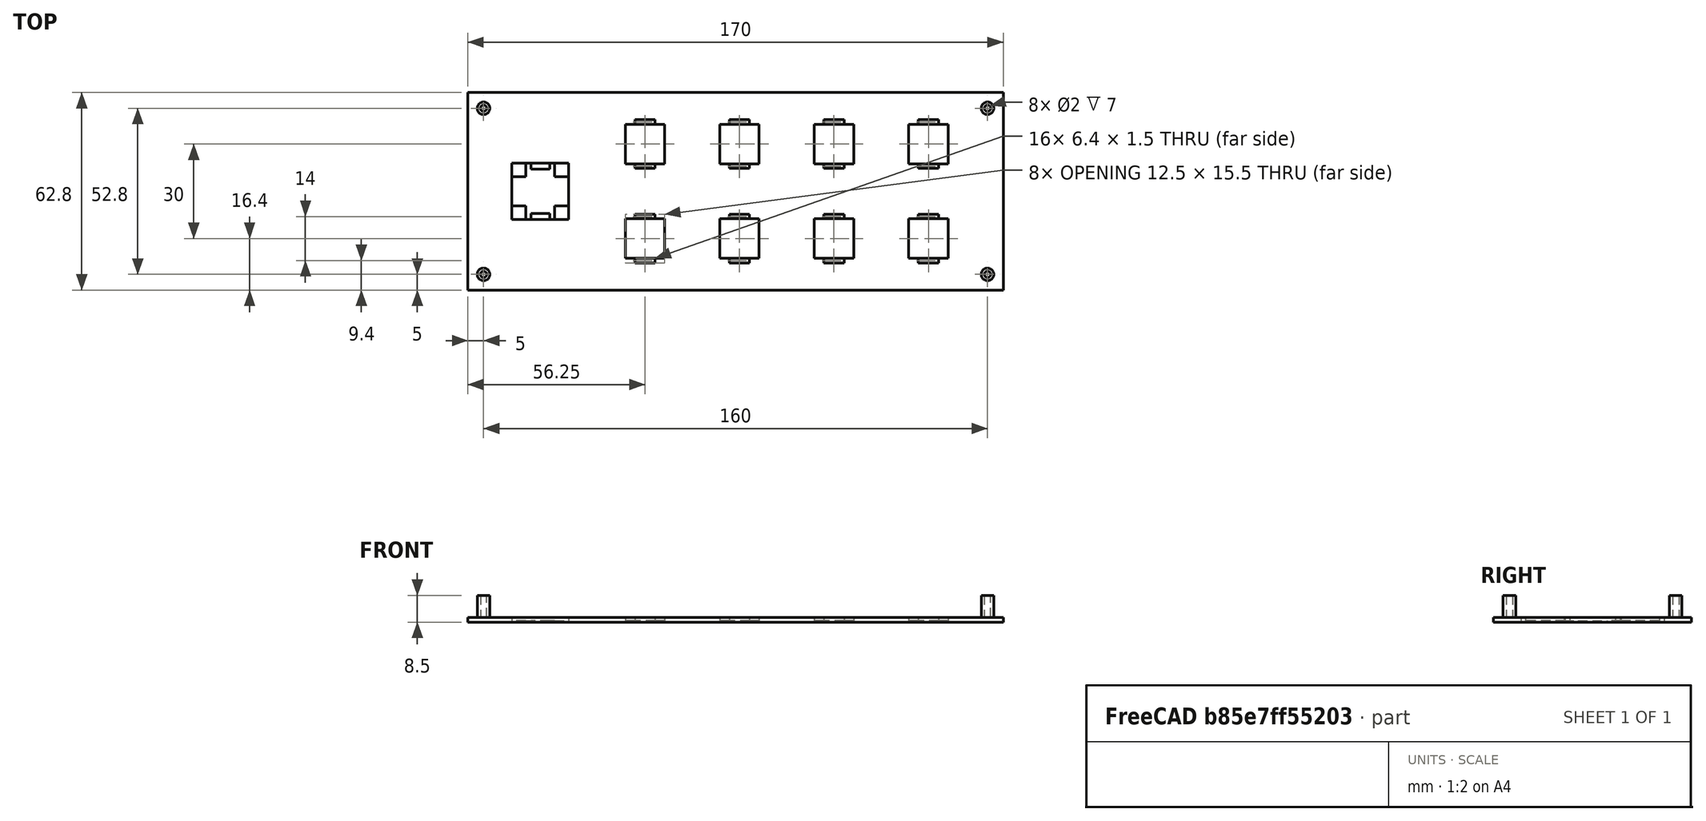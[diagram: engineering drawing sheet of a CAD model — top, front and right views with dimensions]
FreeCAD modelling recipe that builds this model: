
FCSTD DOCUMENT  (FreeCAD 0.20R28671 (Git))
Label: soporte botones atras
License: All rights reserved
LicenseURL: http://en.wikipedia.org/wiki/All_rights_reserved
objects: TechDraw::DrawViewDimension×23, Sketcher::SketchObject×6, PartDesign::Pocket×4, PartDesign::Pad×2, TechDraw::DrawProjGroupItem×2, PartDesign::LinearPattern×1, PartDesign::Body×1, Part::Refine×1, TechDraw::DrawProjGroup×1, TechDraw::DrawSVGTemplate×1, TechDraw::DrawViewAnnotation×1, TechDraw::DrawViewSymbol×1, TechDraw::DrawPage×1
note: 21 computed .brp shape members not serialized (recipe doc carries the construction recipe); baked Part::Feature solids carry a one-line shape summary decoded from their .brp

FEATURE [Sketcher::SketchObject] Sketch
  FullyConstrained = true
  MapMode = 5
  Support = -> [XY_Plane]
  sketch-geometry (12):
    g0: LineSegment StartX=0 StartY=0 StartZ=0 EndX=170 EndY=0 EndZ=0
    g1: LineSegment StartX=170 StartY=0 StartZ=0 EndX=170 EndY=62.8 EndZ=0
    g2: LineSegment StartX=170 StartY=62.8 StartZ=0 EndX=0 EndY=62.8 EndZ=0
    g3: LineSegment StartX=0 StartY=62.8 StartZ=0 EndX=0 EndY=0 EndZ=0
    g4: LineSegment StartX=14 StartY=40.4 StartZ=0 EndX=32 EndY=40.4 EndZ=0
    g5: LineSegment StartX=32 StartY=40.4 StartZ=0 EndX=32 EndY=22.4 EndZ=0
    g6: LineSegment StartX=32 StartY=22.4 StartZ=0 EndX=14 EndY=22.4 EndZ=0
    g7: LineSegment StartX=14 StartY=22.4 StartZ=0 EndX=14 EndY=40.4 EndZ=0
    g8: LineSegment StartX=14 StartY=40.4 StartZ=0 EndX=23 EndY=31.4 EndZ=0
    g9: LineSegment StartX=23 StartY=31.4 StartZ=0 EndX=32 EndY=22.4 EndZ=0
    g10: LineSegment StartX=0 StartY=0 StartZ=0 EndX=0 EndY=31.4 EndZ=0
    g11: LineSegment StartX=0 StartY=62.8 StartZ=0 EndX=0 EndY=31.4 EndZ=0
  constraints (33):
    c: Coincident(g0,g1)
    c: Coincident(g1,g2)
    c: Coincident(g2,g3)
    c: Coincident(g3,g0)
    c: Horizontal(g0)
    c: Horizontal(g2)
    c: Vertical(g1)
    c: Vertical(g3)
    c: Coincident(g0,g-1)
    c: DistanceY(g3,g3) = 62.8
    c: DistanceX(g0,g0) = 170
    c: Coincident(g4,g5)
    c: Coincident(g5,g6)
    c: Coincident(g6,g7)
    c: Coincident(g7,g4)
    c: Horizontal(g4)
    c: Horizontal(g6)
    c: Vertical(g5)
    c: Vertical(g7)
    c: Coincident(g8,g4)
    c: Coincident(g9,g8)
    c: Coincident(g9,g5)
    c: Parallel(g9,g8)
    c: Equal(g8,g9)
    c: Coincident(g10,g0)
    c: Coincident(g11,g2)
    c: Coincident(g11,g10)
    c: Horizontal(g10,g8)
    c: Equal(g6,g7)
    c: DistanceX(g6,g6) = 18
    c: Equal(g10,g11)
    c: Vertical(g10)
    c: DistanceX(g10,g6) = 14
FEATURE [PartDesign::Pad] Pad
  Direction = (0,0,1)
  Length = 1.5
  Length2 = 100
  Profile = -> Sketch
  ReferenceAxis = -> Sketch [N_Axis]
  Type = 0
FEATURE [Sketcher::SketchObject] Sketch001
  FullyConstrained = true
  MapMode = 5
  Placement = pos=(0,0,1.5) rot=(0,0,1;0rad)
  Support = -> [Pad]
  expr: Constraints[10] = Sketch.Constraints[10]
  expr: Constraints[29] = Sketch.Constraints[29]
  expr: Constraints[32] = Sketch.Constraints[32]
  expr: Constraints[9] = Sketch.Constraints[9]
  sketch-geometry (12):
    g0: LineSegment StartX=0 StartY=0 StartZ=0 EndX=170 EndY=0 EndZ=0
    g1: LineSegment StartX=170 StartY=0 StartZ=0 EndX=170 EndY=62.8 EndZ=0
    g2: LineSegment StartX=170 StartY=62.8 StartZ=0 EndX=0 EndY=62.8 EndZ=0
    g3: LineSegment StartX=0 StartY=62.8 StartZ=0 EndX=0 EndY=0 EndZ=0
    g4: LineSegment StartX=14 StartY=40.4 StartZ=0 EndX=32 EndY=40.4 EndZ=0
    g5: LineSegment StartX=32 StartY=40.4 StartZ=0 EndX=32 EndY=22.4 EndZ=0
    g6: LineSegment StartX=32 StartY=22.4 StartZ=0 EndX=14 EndY=22.4 EndZ=0
    g7: LineSegment StartX=14 StartY=22.4 StartZ=0 EndX=14 EndY=40.4 EndZ=0
    g8: LineSegment StartX=14 StartY=40.4 StartZ=0 EndX=23 EndY=31.4 EndZ=0
    g9: LineSegment StartX=23 StartY=31.4 StartZ=0 EndX=32 EndY=22.4 EndZ=0
    g10: LineSegment StartX=0 StartY=0 StartZ=0 EndX=0 EndY=31.4 EndZ=0
    g11: LineSegment StartX=0 StartY=62.8 StartZ=0 EndX=0 EndY=31.4 EndZ=0
  constraints (33):
    c: Coincident(g0,g1)
    c: Coincident(g1,g2)
    c: Coincident(g2,g3)
    c: Coincident(g3,g0)
    c: Horizontal(g0)
    c: Horizontal(g2)
    c: Vertical(g1)
    c: Vertical(g3)
    c: Coincident(g0,g-1)
    c: DistanceY(g3,g3) = 62.8
    c: DistanceX(g0,g0) = 170
    c: Coincident(g4,g5)
    c: Coincident(g5,g6)
    c: Coincident(g6,g7)
    c: Coincident(g7,g4)
    c: Horizontal(g4)
    c: Horizontal(g6)
    c: Vertical(g5)
    c: Vertical(g7)
    c: Coincident(g8,g4)
    c: Coincident(g9,g8)
    c: Coincident(g9,g5)
    c: Parallel(g9,g8)
    c: Equal(g8,g9)
    c: Coincident(g10,g0)
    c: Coincident(g11,g2)
    c: Coincident(g11,g10)
    c: Horizontal(g10,g8)
    c: Equal(g6,g7)
    c: DistanceX(g6,g6) = 18
    c: Equal(g10,g11)
    c: Vertical(g10)
    c: DistanceX(g10,g6) = 14
FEATURE [PartDesign::Pocket] Pocket
  BaseFeature = -> Pad
  Direction = (0,0,-1)
  Length = 1
  Length2 = 100
  Profile = -> Sketch001
  Type = 0
FEATURE [Sketcher::SketchObject] Sketch002
  ExternalGeometry = -> [Pocket]
  FullyConstrained = true
  MapMode = 5
  Placement = pos=(0,0,1.5) rot=(0,0,1;0rad)
  Support = -> [Pocket]
  sketch-geometry (25):
    g0: LineSegment StartX=50 StartY=52.65 StartZ=0 EndX=62.5 EndY=52.65 EndZ=0
    g1: LineSegment StartX=62.5 StartY=52.65 StartZ=0 EndX=62.5 EndY=40.15 EndZ=0
    g2: LineSegment StartX=62.5 StartY=40.15 StartZ=0 EndX=50 EndY=40.15 EndZ=0
    g3: LineSegment StartX=50 StartY=40.15 StartZ=0 EndX=50 EndY=52.65 EndZ=0
    g4: LineSegment StartX=80 StartY=52.65 StartZ=0 EndX=92.5 EndY=52.65 EndZ=0
    g5: LineSegment StartX=92.5 StartY=52.65 StartZ=0 EndX=92.5 EndY=40.15 EndZ=0
    g6: LineSegment StartX=80 StartY=40.15 StartZ=0 EndX=80 EndY=52.65 EndZ=0
    g7: LineSegment StartX=92.5 StartY=40.15 StartZ=0 EndX=80 EndY=40.15 EndZ=0
    g8: LineSegment StartX=50 StartY=52.65 StartZ=0 EndX=80 EndY=52.65 EndZ=0
    g9: LineSegment StartX=50 StartY=22.65 StartZ=0 EndX=62.5 EndY=22.65 EndZ=0
    g10: LineSegment StartX=62.5 StartY=22.65 StartZ=0 EndX=62.5 EndY=10.15 EndZ=0
    g11: LineSegment StartX=50 StartY=10.15 StartZ=0 EndX=50 EndY=22.65 EndZ=0
    g12: LineSegment StartX=62.5 StartY=10.15 StartZ=0 EndX=50 EndY=10.15 EndZ=0
    g13: LineSegment StartX=50 StartY=52.65 StartZ=0 EndX=50 EndY=22.65 EndZ=0
    g14: LineSegment StartX=80 StartY=22.65 StartZ=0 EndX=92.5 EndY=22.65 EndZ=0
    g15: LineSegment StartX=92.5 StartY=22.65 StartZ=0 EndX=92.5 EndY=10.15 EndZ=0
    g16: LineSegment StartX=80 StartY=10.15 StartZ=0 EndX=80 EndY=22.65 EndZ=0
    g17: LineSegment StartX=92.5 StartY=10.15 StartZ=0 EndX=80 EndY=10.15 EndZ=0
    g18: LineSegment StartX=50 StartY=22.65 StartZ=0 EndX=80 EndY=22.65 EndZ=0
    g19: LineSegment StartX=62.5 StartY=40.15 StartZ=0 EndX=62.5 EndY=31.4 EndZ=0
    g20: LineSegment StartX=62.5 StartY=31.4 StartZ=0 EndX=62.5 EndY=22.65 EndZ=0
    g21: LineSegment StartX=32 StartY=40.4 StartZ=0 EndX=32 EndY=31.4 EndZ=0
    g22: LineSegment StartX=32 StartY=31.4 StartZ=0 EndX=32 EndY=22.4 EndZ=0
    g23: LineSegment StartX=50 StartY=40.15 StartZ=0 EndX=32 EndY=40.15 EndZ=0
    g24: LineSegment StartX=32 StartY=40.4 StartZ=0 EndX=32 EndY=22.4 EndZ=0
  constraints (69):
    c: Coincident(g0,g1)
    c: Coincident(g1,g2)
    c: Coincident(g2,g3)
    c: Coincident(g3,g0)
    c: Horizontal(g0)
    c: Horizontal(g2)
    c: Vertical(g1)
    c: Vertical(g3)
    c: Equal(g0,g1)
    c: Coincident(g4,g5)
    c: Coincident(g5,g7)
    c: Coincident(g7,g6)
    c: Coincident(g6,g4)
    c: Horizontal(g4)
    c: Horizontal(g7)
    c: Vertical(g5)
    c: Vertical(g6)
    c: Equal(g4,g5)
    c: Coincident(g0,g8)
    c: Coincident(g4,g8)
    c: Angle(g8) = 0
    c: Coincident(g9,g10)
    c: Coincident(g10,g12)
    c: Coincident(g12,g11)
    c: Coincident(g11,g9)
    c: Horizontal(g9)
    c: Horizontal(g12)
    c: Vertical(g10)
    c: Vertical(g11)
    c: DistanceX(g12,g12) = 12.5
    c: Equal(g9,g10)
    c: Coincident(g0,g13)
    c: Coincident(g9,g13)
    c: Perpendicular(g13,g8)
    c: Coincident(g14,g15)
    c: Coincident(g15,g17)
    c: Coincident(g17,g16)
    c: Coincident(g16,g14)
    c: Horizontal(g14)
    c: Horizontal(g17)
    c: Vertical(g15)
    c: Vertical(g16)
    c: Equal(g14,g15)
    c: Coincident(g9,g18)
    c: Coincident(g14,g18)
    c: Equal(g8,g18)
    c: Parallel(g18,g8)
    c: Vertical(g14,g5)
    c: Vertical(g1,g9)
    c: Coincident(g19,g1)
    c: Coincident(g20,g19)
    c: Coincident(g20,g9)
    c: Equal(g20,g19)
    c: Vertical(g20)
    c: Equal(g17,g12)
    c: DistanceY(g11,g2) = 30
    c: DistanceX(g11,g16) = 30
    c: Coincident(g21,g-3)
    c: Coincident(g22,g21)
    c: Coincident(g22,g-4)
    c: Horizontal(g21,g19)
    c: Equal(g22,g21)
    c: Vertical(g22)
    c: Coincident(g23,g2)
    c: Horizontal(g23)
    c: PointOnObject(g23,g21)
    c: Coincident(g24,g21)
    c: Equal(g24,g23)
    c: Coincident(g24,g22)
FEATURE [PartDesign::Pocket] Pocket001
  BaseFeature = -> Pocket
  Direction = (0,0,-1)
  Length = 1
  Length2 = 100
  Profile = -> Sketch002
  Type = 0
FEATURE [PartDesign::LinearPattern] LinearPattern
  BaseFeature = -> Pocket001
  Direction = -> Sketch002 [Axis0]
  Length = 60
  Occurrences = 2
  Originals = -> [Pocket001]
  Overlap = 0
FEATURE [Sketcher::SketchObject] Sketch003
  ExternalGeometry = -> [LinearPattern]
  FullyConstrained = true
  MapMode = 5
  Placement = pos=(0,0,1.5) rot=(0,0,1;0rad)
  Support = -> [LinearPattern]
  sketch-geometry (16):
    g0: Circle CenterX=5 CenterY=5 CenterZ=0 NormalX=0 NormalY=0 NormalZ=1 AngleXU=0 Radius=1
    g1: Circle CenterX=5 CenterY=5 CenterZ=0 NormalX=0 NormalY=0 NormalZ=1 AngleXU=0 Radius=2
    g2: Circle CenterX=5 CenterY=57.8 CenterZ=0 NormalX=0 NormalY=0 NormalZ=1 AngleXU=0 Radius=1
    g3: Circle CenterX=5 CenterY=57.8 CenterZ=0 NormalX=0 NormalY=0 NormalZ=1 AngleXU=0 Radius=2
    g4: Circle CenterX=165 CenterY=57.8 CenterZ=0 NormalX=0 NormalY=0 NormalZ=1 AngleXU=0 Radius=2
    g5: Circle CenterX=165 CenterY=57.8 CenterZ=0 NormalX=0 NormalY=0 NormalZ=1 AngleXU=0 Radius=1
    g6: Circle CenterX=165 CenterY=5 CenterZ=0 NormalX=0 NormalY=0 NormalZ=1 AngleXU=0 Radius=2
    g7: Circle CenterX=165 CenterY=5 CenterZ=0 NormalX=0 NormalY=0 NormalZ=1 AngleXU=0 Radius=1
    g8: LineSegment StartX=0 StartY=0 StartZ=0 EndX=5 EndY=0 EndZ=0
    g9: LineSegment StartX=5 StartY=0 StartZ=0 EndX=5 EndY=5 EndZ=0
    g10: LineSegment StartX=165 StartY=5 StartZ=0 EndX=165 EndY=0 EndZ=0
    g11: LineSegment StartX=165 StartY=0 StartZ=0 EndX=170 EndY=0 EndZ=0
    g12: LineSegment StartX=165 StartY=57.8 StartZ=0 EndX=165 EndY=62.8 EndZ=0
    g13: LineSegment StartX=165 StartY=62.8 StartZ=0 EndX=170 EndY=62.8 EndZ=0
    g14: LineSegment StartX=5 StartY=57.8 StartZ=0 EndX=0 EndY=57.8 EndZ=0
    g15: LineSegment StartX=0 StartY=57.8 StartZ=0 EndX=0 EndY=62.8 EndZ=0
  constraints (40):
    c: Coincident(g1,g0)
    c: Diameter(g0) = 2
    c: Diameter(g1) = 4
    c: DistanceY(g-1,g0) = 5
    c: DistanceX(g-1,g0) = 5
    c: Coincident(g3,g2)
    c: Coincident(g5,g4)
    c: Coincident(g7,g6)
    c: Equal(g2,g5)
    c: Equal(g5,g7)
    c: Equal(g7,g0)
    c: Equal(g1,g6)
    c: Equal(g6,g4)
    c: Equal(g4,g3)
    c: Coincident(g8,g-1)
    c: PointOnObject(g8,g-1)
    c: Coincident(g9,g8)
    c: Coincident(g9,g0)
    c: Vertical(g9)
    c: Coincident(g10,g6)
    c: PointOnObject(g10,g-1)
    c: Vertical(g10)
    c: Coincident(g11,g10)
    c: Coincident(g11,g-5)
    c: Coincident(g12,g4)
    c: Vertical(g12)
    c: Coincident(g13,g12)
    c: Coincident(g13,g-4)
    c: Horizontal(g13)
    c: Coincident(g14,g2)
    c: PointOnObject(g14,g-2)
    c: Horizontal(g14)
    c: Coincident(g15,g14)
    c: Coincident(g15,g-3)
    c: Equal(g14,g15)
    c: Equal(g15,g8)
    c: Equal(g11,g10)
    c: Equal(g10,g13)
    c: Equal(g13,g12)
    c: Equal(g12,g8)
FEATURE [PartDesign::Pad] Pad001
  BaseFeature = -> LinearPattern
  Direction = (0,0,1)
  Length = 7
  Length2 = 100
  Profile = -> Sketch003
  ReferenceAxis = -> Sketch003 [N_Axis]
  Type = 0
FEATURE [Sketcher::SketchObject] Sketch004
  ExternalGeometry = -> [Pad001]
  FullyConstrained = true
  MapMode = 5
  Placement = pos=(0,0,1.5) rot=(0,0,1;0rad)
  Support = -> [Pad001]
  sketch-geometry (73):
    g0: LineSegment StartX=53.05 StartY=54.15 StartZ=0 EndX=59.45 EndY=54.15 EndZ=0
    g1: LineSegment StartX=59.45 StartY=54.15 StartZ=0 EndX=59.45 EndY=52.65 EndZ=0
    g2: LineSegment StartX=59.45 StartY=52.65 StartZ=0 EndX=53.05 EndY=52.65 EndZ=0
    g3: LineSegment StartX=53.05 StartY=52.65 StartZ=0 EndX=53.05 EndY=54.15 EndZ=0
    g4: LineSegment StartX=53.05 StartY=40.15 StartZ=0 EndX=59.45 EndY=40.15 EndZ=0
    g5: LineSegment StartX=59.45 StartY=40.15 StartZ=0 EndX=59.45 EndY=38.65 EndZ=0
    g6: LineSegment StartX=59.45 StartY=38.65 StartZ=0 EndX=53.05 EndY=38.65 EndZ=0
    g7: LineSegment StartX=53.05 StartY=38.65 StartZ=0 EndX=53.05 EndY=40.15 EndZ=0
    g8: LineSegment StartX=53.05 StartY=52.65 StartZ=0 EndX=50 EndY=52.65 EndZ=0
    g9: LineSegment StartX=62.5 StartY=52.65 StartZ=0 EndX=59.45 EndY=52.65 EndZ=0
    g10: LineSegment StartX=83.05 StartY=38.65 StartZ=0 EndX=83.05 EndY=40.15 EndZ=0
    g11: LineSegment StartX=89.45 StartY=38.65 StartZ=0 EndX=83.05 EndY=38.65 EndZ=0
    g12: LineSegment StartX=89.45 StartY=40.15 StartZ=0 EndX=89.45 EndY=38.65 EndZ=0
    g13: LineSegment StartX=83.05 StartY=40.15 StartZ=0 EndX=89.45 EndY=40.15 EndZ=0
    g14: LineSegment StartX=89.45 StartY=52.65 StartZ=0 EndX=83.05 EndY=52.65 EndZ=0
    g15: LineSegment StartX=83.05 StartY=54.15 StartZ=0 EndX=89.45 EndY=54.15 EndZ=0
    g16: LineSegment StartX=89.45 StartY=54.15 StartZ=0 EndX=89.45 EndY=52.65 EndZ=0
    g17: LineSegment StartX=83.05 StartY=52.65 StartZ=0 EndX=83.05 EndY=54.15 EndZ=0
    g18: LineSegment StartX=53.05 StartY=38.65 StartZ=0 EndX=83.05 EndY=38.65 EndZ=0
    g19: LineSegment StartX=113.05 StartY=38.65 StartZ=0 EndX=113.05 EndY=40.15 EndZ=0
    g20: LineSegment StartX=119.45 StartY=38.65 StartZ=0 EndX=113.05 EndY=38.65 EndZ=0
    g21: LineSegment StartX=119.45 StartY=40.15 StartZ=0 EndX=119.45 EndY=38.65 EndZ=0
    g22: LineSegment StartX=113.05 StartY=40.15 StartZ=0 EndX=119.45 EndY=40.15 EndZ=0
    g23: LineSegment StartX=119.45 StartY=52.65 StartZ=0 EndX=113.05 EndY=52.65 EndZ=0
    g24: LineSegment StartX=113.05 StartY=54.15 StartZ=0 EndX=119.45 EndY=54.15 EndZ=0
    g25: LineSegment StartX=119.45 StartY=54.15 StartZ=0 EndX=119.45 EndY=52.65 EndZ=0
    g26: LineSegment StartX=113.05 StartY=52.65 StartZ=0 EndX=113.05 EndY=54.15 EndZ=0
    g27: LineSegment StartX=83.05 StartY=38.65 StartZ=0 EndX=113.05 EndY=38.65 EndZ=0
    g28: LineSegment StartX=143.05 StartY=38.65 StartZ=0 EndX=143.05 EndY=40.15 EndZ=0
    g29: LineSegment StartX=149.45 StartY=38.65 StartZ=0 EndX=143.05 EndY=38.65 EndZ=0
    g30: LineSegment StartX=149.45 StartY=40.15 StartZ=0 EndX=149.45 EndY=38.65 EndZ=0
    g31: LineSegment StartX=143.05 StartY=40.15 StartZ=0 EndX=149.45 EndY=40.15 EndZ=0
    g32: LineSegment StartX=149.45 StartY=52.65 StartZ=0 EndX=143.05 EndY=52.65 EndZ=0
    g33: LineSegment StartX=143.05 StartY=54.15 StartZ=0 EndX=149.45 EndY=54.15 EndZ=0
    g34: LineSegment StartX=149.45 StartY=54.15 StartZ=0 EndX=149.45 EndY=52.65 EndZ=0
    g35: LineSegment StartX=143.05 StartY=52.65 StartZ=0 EndX=143.05 EndY=54.15 EndZ=0
    g36: LineSegment StartX=113.05 StartY=38.65 StartZ=0 EndX=143.05 EndY=38.65 EndZ=0
    g37: LineSegment StartX=83.05 StartY=40.15 StartZ=0 EndX=80 EndY=40.15 EndZ=0
    g38: LineSegment StartX=32 StartY=40.4 StartZ=0 EndX=32 EndY=31.4 EndZ=0
    g39: LineSegment StartX=32 StartY=31.4 StartZ=0 EndX=32 EndY=22.4 EndZ=0
    g40: LineSegment StartX=32 StartY=31.4 StartZ=0 EndX=170 EndY=31.4 EndZ=0
    g41: LineSegment StartX=59.45 StartY=24.15 StartZ=0 EndX=53.05 EndY=24.15 EndZ=0
    g42: LineSegment StartX=53.05 StartY=24.15 StartZ=0 EndX=53.05 EndY=22.65 EndZ=0
    g43: LineSegment StartX=53.05 StartY=22.65 StartZ=0 EndX=59.45 EndY=22.65 EndZ=0
    g44: LineSegment StartX=59.45 StartY=22.65 StartZ=0 EndX=59.45 EndY=24.15 EndZ=0
    g45: LineSegment StartX=53.05 StartY=8.65 StartZ=0 EndX=59.45 EndY=8.65 EndZ=0
    g46: LineSegment StartX=59.45 StartY=8.65 StartZ=0 EndX=59.45 EndY=10.15 EndZ=0
    g47: LineSegment StartX=59.45 StartY=10.15 StartZ=0 EndX=53.05 EndY=10.15 EndZ=0
    g48: LineSegment StartX=53.05 StartY=10.15 StartZ=0 EndX=53.05 EndY=8.65 EndZ=0
    g49: LineSegment StartX=83.05 StartY=8.65 StartZ=0 EndX=89.45 EndY=8.65 EndZ=0
    g50: LineSegment StartX=83.05 StartY=10.15 StartZ=0 EndX=83.05 EndY=8.65 EndZ=0
    g51: LineSegment StartX=89.45 StartY=10.15 StartZ=0 EndX=83.05 EndY=10.15 EndZ=0
    g52: LineSegment StartX=89.45 StartY=8.65 StartZ=0 EndX=89.45 EndY=10.15 EndZ=0
    g53: LineSegment StartX=83.05 StartY=22.65 StartZ=0 EndX=89.45 EndY=22.65 EndZ=0
    g54: LineSegment StartX=89.45 StartY=24.15 StartZ=0 EndX=83.05 EndY=24.15 EndZ=0
    g55: LineSegment StartX=83.05 StartY=24.15 StartZ=0 EndX=83.05 EndY=22.65 EndZ=0
    g56: LineSegment StartX=89.45 StartY=22.65 StartZ=0 EndX=89.45 EndY=24.15 EndZ=0
    g57: LineSegment StartX=113.05 StartY=8.65 StartZ=0 EndX=119.45 EndY=8.65 EndZ=0
    g58: LineSegment StartX=119.45 StartY=10.15 StartZ=0 EndX=113.05 EndY=10.15 EndZ=0
    g59: LineSegment StartX=113.05 StartY=10.15 StartZ=0 EndX=113.05 EndY=8.65 EndZ=0
    g60: LineSegment StartX=119.45 StartY=8.65 StartZ=0 EndX=119.45 EndY=10.15 EndZ=0
    g61: LineSegment StartX=113.05 StartY=22.65 StartZ=0 EndX=119.45 EndY=22.65 EndZ=0
    g62: LineSegment StartX=119.45 StartY=22.65 StartZ=0 EndX=119.45 EndY=24.15 EndZ=0
    g63: LineSegment StartX=119.45 StartY=24.15 StartZ=0 EndX=113.05 EndY=24.15 EndZ=0
    g64: LineSegment StartX=113.05 StartY=24.15 StartZ=0 EndX=113.05 EndY=22.65 EndZ=0
    g65: LineSegment StartX=143.05 StartY=8.65 StartZ=0 EndX=149.45 EndY=8.65 EndZ=0
    g66: LineSegment StartX=149.45 StartY=10.15 StartZ=0 EndX=143.05 EndY=10.15 EndZ=0
    g67: LineSegment StartX=143.05 StartY=10.15 StartZ=0 EndX=143.05 EndY=8.65 EndZ=0
    g68: LineSegment StartX=149.45 StartY=8.65 StartZ=0 EndX=149.45 EndY=10.15 EndZ=0
    g69: LineSegment StartX=143.05 StartY=22.65 StartZ=0 EndX=149.45 EndY=22.65 EndZ=0
    g70: LineSegment StartX=143.05 StartY=24.15 StartZ=0 EndX=143.05 EndY=22.65 EndZ=0
    g71: LineSegment StartX=149.45 StartY=24.15 StartZ=0 EndX=143.05 EndY=24.15 EndZ=0
    g72: LineSegment StartX=149.45 StartY=22.65 StartZ=0 EndX=149.45 EndY=24.15 EndZ=0
  constraints (212):
    c: Coincident(g0,g1)
    c: Coincident(g1,g2)
    c: Coincident(g2,g3)
    c: Coincident(g3,g0)
    c: Horizontal(g0)
    c: Horizontal(g2)
    c: Vertical(g1)
    c: Vertical(g3)
    c: Coincident(g4,g5)
    c: Coincident(g5,g6)
    c: Coincident(g6,g7)
    c: Coincident(g7,g4)
    c: Horizontal(g4)
    c: Horizontal(g6)
    c: Vertical(g5)
    c: Vertical(g7)
    c: Vertical(g2,g4)
    c: Vertical(g4,g1)
    c: Equal(g7,g3)
    c: Coincident(g8,g2)
    c: Coincident(g8,g-3)
    c: Coincident(g9,g-4)
    c: Coincident(g9,g1)
    c: Equal(g8,g9)
    c: Horizontal(g9)
    c: DistanceX(g0,g0) = 6.4
    c: DistanceY(g3,g3) = 1.5
    c: Horizontal(g4,g-6)
    c: Coincident(g15,g16)
    c: Coincident(g16,g14)
    c: Coincident(g14,g17)
    c: Coincident(g17,g15)
    c: Horizontal(g15)
    c: Horizontal(g14)
    c: Vertical(g16)
    c: Vertical(g17)
    c: Coincident(g13,g12)
    c: Coincident(g12,g11)
    c: Coincident(g11,g10)
    c: Coincident(g10,g13)
    c: Horizontal(g13)
    c: Horizontal(g11)
    c: Vertical(g12)
    c: Vertical(g10)
    c: Vertical(g14,g13)
    c: Vertical(g13,g16)
    c: Equal(g10,g17)
    c: Coincident(g7,g18)
    c: Coincident(g10,g18)
    c: Coincident(g24,g25)
    c: Coincident(g25,g23)
    c: Coincident(g23,g26)
    c: Coincident(g26,g24)
    c: Horizontal(g24)
    c: Horizontal(g23)
    c: Vertical(g25)
    c: Vertical(g26)
    c: Coincident(g22,g21)
    c: Coincident(g21,g20)
    c: Coincident(g20,g19)
    c: Coincident(g19,g22)
    c: Horizontal(g22)
    c: Horizontal(g20)
    c: Vertical(g21)
    c: Vertical(g19)
    c: Vertical(g23,g22)
    c: Vertical(g22,g25)
    c: Equal(g19,g26)
    c: Coincident(g10,g27)
    c: Coincident(g19,g27)
    c: Equal(g18,g27)
    c: Parallel(g27,g18)
    c: Coincident(g33,g34)
    c: Coincident(g34,g32)
    c: Coincident(g32,g35)
    c: Coincident(g35,g33)
    c: Horizontal(g33)
    c: Horizontal(g32)
    c: Vertical(g34)
    c: Vertical(g35)
    c: Coincident(g31,g30)
    c: Coincident(g30,g29)
    c: Coincident(g29,g28)
    c: Coincident(g28,g31)
    c: Horizontal(g31)
    c: Horizontal(g29)
    c: Vertical(g30)
    c: Vertical(g28)
    c: Vertical(g32,g31)
    c: Vertical(g31,g34)
    c: Equal(g28,g35)
    c: Coincident(g19,g36)
    c: Coincident(g28,g36)
    c: Equal(g18,g36)
    c: Parallel(g36,g18)
    c: Coincident(g37,g10)
    c: Coincident(g37,g-7)
    c: Equal(g37,g9)
    c: Horizontal(g37)
    c: Equal(g15,g0)
    c: Equal(g0,g24)
    c: Equal(g24,g33)
    c: Horizontal(g36)
    c: Equal(g12,g19)
    c: Equal(g19,g30)
    c: Horizontal(g14,g9)
    c: Horizontal(g23,g32)
    c: Horizontal(g23,g14)
    c: Coincident(g38,g-8)
    c: Coincident(g39,g38)
    c: Coincident(g39,g-9)
    c: Equal(g39,g38)
    c: Vertical(g39)
    c: Coincident(g40,g38)
    c: Horizontal(g40)
    c: Vertical(g-10,g40)
    c: Coincident(g45,g46)
    c: Coincident(g46,g47)
    c: Coincident(g47,g48)
    c: Coincident(g48,g45)
    c: Horizontal(g45)
    c: Horizontal(g47)
    c: Vertical(g46)
    c: Vertical(g48)
    c: Coincident(g43,g44)
    c: Coincident(g44,g41)
    c: Coincident(g41,g42)
    c: Coincident(g42,g43)
    c: Horizontal(g43)
    c: Horizontal(g41)
    c: Vertical(g44)
    c: Vertical(g42)
    c: Equal(g42,g48)
    c: Coincident(g49,g52)
    c: Coincident(g52,g51)
    c: Coincident(g51,g50)
    c: Coincident(g50,g49)
    c: Horizontal(g49)
    c: Horizontal(g51)
    c: Vertical(g52)
    c: Vertical(g50)
    c: Coincident(g53,g56)
    c: Coincident(g56,g54)
    c: Coincident(g54,g55)
    c: Coincident(g55,g53)
    c: Horizontal(g53)
    c: Horizontal(g54)
    c: Vertical(g56)
    c: Vertical(g55)
    c: Equal(g55,g50)
    c: Coincident(g57,g60)
    c: Coincident(g60,g58)
    c: Coincident(g58,g59)
    c: Coincident(g59,g57)
    c: Horizontal(g57)
    c: Horizontal(g58)
    c: Vertical(g60)
    c: Vertical(g59)
    c: Coincident(g61,g62)
    c: Coincident(g62,g63)
    c: Coincident(g63,g64)
    c: Coincident(g64,g61)
    c: Horizontal(g61)
    c: Horizontal(g63)
    c: Vertical(g62)
    c: Equal(g64,g59)
    c: Coincident(g65,g68)
    c: Coincident(g68,g66)
    c: Coincident(g66,g67)
    c: Coincident(g67,g65)
    c: Horizontal(g65)
    c: Horizontal(g66)
    c: Vertical(g68)
    c: Vertical(g67)
    c: Coincident(g69,g72)
    c: Coincident(g72,g71)
    c: Coincident(g71,g70)
    c: Coincident(g70,g69)
    c: Horizontal(g69)
    c: Horizontal(g71)
    c: Vertical(g72)
    c: Vertical(g70)
    c: Equal(g70,g67)
    c: Equal(g49,g45)
    c: Equal(g45,g57)
    c: Equal(g57,g65)
    c: Equal(g56,g64)
    c: Equal(g64,g72)
    c: Vertical(g41,g6)
    c: Vertical(g54,g10)
    c: Vertical(g63,g19)
    c: Vertical(g70,g28)
    c: Equal(g31,g71)
    c: Equal(g71,g63)
    c: Equal(g63,g54)
    c: Equal(g54,g41)
    c: Equal(g44,g55)
    c: Equal(g55,g62)
    c: Equal(g72,g30)
    c: Horizontal(g43,g-11)
    c: Horizontal(g-11,g53)
    c: Horizontal(g53,g61)
    c: Horizontal(g61,g69)
    c: Horizontal(g46,g-12)
    c: Vertical(g46,g43)
    c: Equal(g47,g43)
    c: Horizontal(g-12,g50)
    c: Horizontal(g51,g58)
    c: Horizontal(g58,g66)
    c: Vertical(g51,g53)
    c: Vertical(g61,g58)
    c: Vertical(g69,g66)
FEATURE [Sketcher::SketchObject] Sketch005
  ExternalGeometry = -> [Pad001]
  FullyConstrained = true
  MapMode = 5
  Placement = pos=(0,0,0.5) rot=(0,0,1;0rad)
  Support = -> [Pad001]
  sketch-geometry (26):
    g0: LineSegment StartX=20 StartY=40.4 StartZ=0 EndX=26 EndY=40.4 EndZ=0
    g1: LineSegment StartX=26 StartY=40.4 StartZ=0 EndX=26 EndY=38.4 EndZ=0
    g2: LineSegment StartX=26 StartY=38.4 StartZ=0 EndX=20 EndY=38.4 EndZ=0
    g3: LineSegment StartX=20 StartY=38.4 StartZ=0 EndX=20 EndY=40.4 EndZ=0
    g4: LineSegment StartX=20 StartY=22.4 StartZ=0 EndX=26 EndY=22.4 EndZ=0
    g5: LineSegment StartX=26 StartY=22.4 StartZ=0 EndX=26 EndY=24.4 EndZ=0
    g6: LineSegment StartX=26 StartY=24.4 StartZ=0 EndX=20 EndY=24.4 EndZ=0
    g7: LineSegment StartX=20 StartY=24.4 StartZ=0 EndX=20 EndY=22.4 EndZ=0
    g8: LineSegment StartX=20 StartY=40.4 StartZ=0 EndX=14 EndY=40.4 EndZ=0
    g9: LineSegment StartX=26 StartY=40.4 StartZ=0 EndX=32 EndY=40.4 EndZ=0
    g10: LineSegment StartX=14 StartY=40.4 StartZ=0 EndX=18.4 EndY=40.4 EndZ=0
    g11: LineSegment StartX=18.4 StartY=40.4 StartZ=0 EndX=18.4 EndY=36 EndZ=0
    g12: LineSegment StartX=18.4 StartY=36 StartZ=0 EndX=14 EndY=36 EndZ=0
    g13: LineSegment StartX=14 StartY=36 StartZ=0 EndX=14 EndY=40.4 EndZ=0
    g14: LineSegment StartX=32 StartY=40.4 StartZ=0 EndX=27.6 EndY=40.4 EndZ=0
    g15: LineSegment StartX=27.6 StartY=40.4 StartZ=0 EndX=27.6 EndY=36 EndZ=0
    g16: LineSegment StartX=27.6 StartY=36 StartZ=0 EndX=32 EndY=36 EndZ=0
    g17: LineSegment StartX=32 StartY=36 StartZ=0 EndX=32 EndY=40.4 EndZ=0
    g18: LineSegment StartX=14 StartY=22.4 StartZ=0 EndX=18.4 EndY=22.4 EndZ=0
    g19: LineSegment StartX=18.4 StartY=22.4 StartZ=0 EndX=18.4 EndY=26.8 EndZ=0
    g20: LineSegment StartX=18.4 StartY=26.8 StartZ=0 EndX=14 EndY=26.8 EndZ=0
    g21: LineSegment StartX=14 StartY=26.8 StartZ=0 EndX=14 EndY=22.4 EndZ=0
    g22: LineSegment StartX=32 StartY=22.4 StartZ=0 EndX=27.6 EndY=22.4 EndZ=0
    g23: LineSegment StartX=27.6 StartY=22.4 StartZ=0 EndX=27.6 EndY=26.8 EndZ=0
    g24: LineSegment StartX=27.6 StartY=26.8 StartZ=0 EndX=32 EndY=26.8 EndZ=0
    g25: LineSegment StartX=32 StartY=26.8 StartZ=0 EndX=32 EndY=22.4 EndZ=0
  constraints (72):
    c: Coincident(g0,g1)
    c: Coincident(g1,g2)
    c: Coincident(g2,g3)
    c: Coincident(g3,g0)
    c: Horizontal(g0)
    c: Horizontal(g2)
    c: Vertical(g1)
    c: Vertical(g3)
    c: Coincident(g4,g5)
    c: Coincident(g5,g6)
    c: Coincident(g6,g7)
    c: Coincident(g7,g4)
    c: Horizontal(g4)
    c: Horizontal(g6)
    c: Vertical(g5)
    c: Vertical(g7)
    c: Vertical(g6,g2)
    c: Vertical(g5,g1)
    c: DistanceX(g2,g2) = 6
    c: DistanceY(g3,g3) = 2
    c: Coincident(g8,g0)
    c: Coincident(g8,g-3)
    c: Horizontal(g8)
    c: Coincident(g9,g0)
    c: Coincident(g9,g-4)
    c: Equal(g9,g8)
    c: Equal(g5,g1)
    c: Horizontal(g4,g-5)
    c: Coincident(g10,g11)
    c: Coincident(g11,g12)
    c: Coincident(g12,g13)
    c: Coincident(g13,g10)
    c: Horizontal(g10)
    c: Horizontal(g12)
    c: Vertical(g11)
    c: Vertical(g13)
    c: Coincident(g10,g8)
    c: Coincident(g14,g15)
    c: Coincident(g15,g16)
    c: Coincident(g16,g17)
    c: Coincident(g17,g14)
    c: Horizontal(g14)
    c: Horizontal(g16)
    c: Vertical(g15)
    c: Vertical(g17)
    c: Coincident(g14,g9)
    c: Coincident(g18,g19)
    c: Coincident(g19,g20)
    c: Coincident(g20,g21)
    c: Coincident(g21,g18)
    c: Horizontal(g18)
    c: Horizontal(g20)
    c: Vertical(g19)
    c: Vertical(g21)
    c: Coincident(g18,g-6)
    c: Coincident(g22,g23)
    c: Coincident(g23,g24)
    c: Coincident(g24,g25)
    c: Coincident(g25,g22)
    c: Horizontal(g22)
    c: Horizontal(g24)
    c: Vertical(g23)
    c: Vertical(g25)
    c: Coincident(g22,g-5)
    c: Equal(g16,g15)
    c: Equal(g15,g12)
    c: Equal(g12,g11)
    c: Equal(g11,g20)
    c: Equal(g20,g19)
    c: Equal(g19,g23)
    c: Equal(g23,g24)
    c: DistanceY(g19,g11) = 9.2
FEATURE [PartDesign::Pocket] Pocket002
  BaseFeature = -> Pad001
  Direction = (0,0,-1)
  Length = 5
  Length2 = 100
  Profile = -> Sketch004
  Type = 1
FEATURE [PartDesign::Pocket] Pocket003
  BaseFeature = -> Pocket002
  Direction = (0,0,-1)
  Length = 5
  Length2 = 100
  Profile = -> Sketch005
  Type = 1
FEATURE [PartDesign::Body] Body
  Group = -> [Sketch,Pad,Sketch001,Pocket,Sketch002,Pocket001,LinearPattern,Sketch003,Pad001,Sketch004,Sketch005,Pocket002,Pocket003]
  Origin = -> Origin
  Tip = -> Pocket003
FEATURE [Part::Refine] Pocket003001
  Source = -> Pocket003
FEATURE [TechDraw::DrawProjGroupItem] ProjItem003  label="Front001"
  CoarseView = false
  Direction = (0,0,1)
  Focus = 100
  HardHidden = false
  IsoCount = 0
  IsoHidden = false
  IsoVisible = false
  LockPosition = true
  Perspective = false
  Rotation = 0
  RotationVector = (0,1,0)
  ScaleType = 2
  SeamHidden = false
  SeamVisible = true
  SmoothHidden = false
  SmoothVisible = true
  Source = -> [Pocket003001]
  Type = 0
  X = 0
  XDirection = (1,1e-16,0)
  Y = 0
FEATURE [TechDraw::DrawProjGroupItem] ProjItem004  label="Bottom"
  CoarseView = false
  Direction = (1e-16,-1,0)
  Focus = 100
  HardHidden = false
  IsoCount = 0
  IsoHidden = false
  IsoVisible = false
  LockPosition = true
  Perspective = false
  Rotation = 0
  RotationVector = (1,0,0)
  ScaleType = 2
  SeamHidden = false
  SeamVisible = true
  SmoothHidden = false
  SmoothVisible = true
  Source = -> [Pocket003001]
  Type = 5
  X = 0
  XDirection = (1,1e-16,0)
  Y = 76.7883
FEATURE [TechDraw::DrawProjGroup] ProjGroup002
  Anchor = -> ProjItem003
  AutoDistribute = true
  LockPosition = true
  ProjectionType = 0
  Rotation = 0
  ScaleType = 0
  Source = -> [Pocket003001]
  Views = -> [ProjItem003,ProjItem004]
  X = 151.051
  Y = 89.6803
  spacingX = 15
  spacingY = 15
FEATURE [TechDraw::DrawSVGTemplate] Template002
  EditableTexts = AUTHOR_NAME=Daniel García García; DATE=13-04-2022; DN=3; DOCUMENT_TYPE=Plano de Pieza; PN=4; REVISION=1; SCALE=1:1; SHEET=3/15; SIZE=A4; TITLELINE-1=Soporte de Botones Atrás
  Height = 210
  Orientation = 1
  Width = 297
FEATURE [TechDraw::DrawViewAnnotation] Annotation
  Font = osifont
  LineSpace = 80
  LockPosition = false
  MaxWidth = -1
  Rotation = 0
  ScaleType = 0
  Text = Default Text
  TextSize = 5
  TextStyle = 0
  X = 148.5
  Y = 105
FEATURE [TechDraw::DrawViewSymbol] Symbol
  LockPosition = false
  Rotation = 0
  Scale = 0.3
  ScaleType = 2
  Symbol = <blob: 2444 chars omitted>
  X = 217.487
  Y = 36.9001
FEATURE [TechDraw::DrawViewDimension] Dimension
  AngleOverride = false
  Arbitrary = false
  ArbitraryTolerances = false
  EqualTolerance = true
  ExtensionAngle = 0
  FormatSpec = %.2w
  FormatSpecOverTolerance = %+.2w
  FormatSpecUnderTolerance = %+.2w
  Inverted = false
  LineAngle = 0
  LockPosition = false
  MeasureType = 1
  OverTolerance = 0
  References2D = -> [ProjItem004]
  Rotation = 0
  ScaleType = 0
  TheoreticalExact = false
  Type = 1
  UnderTolerance = 0
  X = 0.33961
  Y = 19.9383
FEATURE [TechDraw::DrawViewDimension] Dimension001
  AngleOverride = false
  Arbitrary = false
  ArbitraryTolerances = false
  EqualTolerance = true
  ExtensionAngle = 0
  FormatSpec = %.2w
  FormatSpecOverTolerance = %+.2w
  FormatSpecUnderTolerance = %+.2w
  Inverted = false
  LineAngle = 0
  LockPosition = false
  MeasureType = 1
  OverTolerance = 0
  References2D = -> [ProjItem003]
  Rotation = 0
  ScaleType = 0
  TheoreticalExact = false
  Type = 2
  UnderTolerance = 0
  X = 95.5467
  Y = 2.16039
FEATURE [TechDraw::DrawViewDimension] Dimension002
  AngleOverride = false
  Arbitrary = false
  ArbitraryTolerances = false
  EqualTolerance = true
  ExtensionAngle = 0
  FormatSpec = %.2w
  FormatSpecOverTolerance = %+.2w
  FormatSpecUnderTolerance = %+.2w
  Inverted = false
  LineAngle = 0
  LockPosition = false
  MeasureType = 1
  OverTolerance = 0
  References2D = -> [ProjItem003]
  Rotation = 0
  ScaleType = 0
  TheoreticalExact = false
  Type = 2
  UnderTolerance = 0
  X = -101.301
  Y = 0.801951
FEATURE [TechDraw::DrawViewDimension] Dimension003
  AngleOverride = false
  Arbitrary = false
  ArbitraryTolerances = false
  EqualTolerance = true
  ExtensionAngle = 0
  FormatSpec = %.2w
  FormatSpecOverTolerance = %+.2w
  FormatSpecUnderTolerance = %+.2w
  Inverted = false
  LineAngle = 0
  LockPosition = false
  MeasureType = 1
  OverTolerance = 0
  References2D = -> [ProjItem004]
  Rotation = 0
  ScaleType = 0
  TheoreticalExact = false
  Type = 1
  UnderTolerance = 0
  X = -1.29175
  Y = -9.71579
FEATURE [TechDraw::DrawViewDimension] Dimension004
  AngleOverride = false
  Arbitrary = false
  ArbitraryTolerances = false
  EqualTolerance = true
  ExtensionAngle = 0
  FormatSpec = %.2w
  FormatSpecOverTolerance = %+.2w
  FormatSpecUnderTolerance = %+.2w
  Inverted = false
  LineAngle = 0
  LockPosition = false
  MeasureType = 1
  OverTolerance = 0
  References2D = -> [ProjItem004]
  Rotation = 0
  ScaleType = 0
  TheoreticalExact = false
  Type = 2
  UnderTolerance = 0
  X = 92.1046
  Y = -1.21529
FEATURE [TechDraw::DrawViewDimension] Dimension005
  AngleOverride = false
  Arbitrary = false
  ArbitraryTolerances = false
  EqualTolerance = true
  ExtensionAngle = 0
  FormatSpec = %.2w
  FormatSpecOverTolerance = %+.2w
  FormatSpecUnderTolerance = %+.2w
  Inverted = false
  LineAngle = 0
  LockPosition = false
  MeasureType = 1
  OverTolerance = 0
  References2D = -> [ProjItem004]
  Rotation = 0
  ScaleType = 0
  TheoreticalExact = false
  Type = 2
  UnderTolerance = 0
  X = -90.1413
  Y = 13.6156
FEATURE [TechDraw::DrawViewDimension] Dimension006
  AngleOverride = false
  Arbitrary = false
  ArbitraryTolerances = false
  EqualTolerance = true
  ExtensionAngle = 0
  FormatSpec = ⌀%.2w
  FormatSpecOverTolerance = %+.2w
  FormatSpecUnderTolerance = %+.2w
  Inverted = false
  LineAngle = 0
  LockPosition = false
  MeasureType = 1
  OverTolerance = 0
  References2D = -> [ProjItem003]
  Rotation = 0
  ScaleType = 0
  TheoreticalExact = false
  Type = 5
  UnderTolerance = 0
  X = -59.7789
  Y = 42.0909
FEATURE [TechDraw::DrawViewDimension] Dimension007
  AngleOverride = false
  Arbitrary = false
  ArbitraryTolerances = false
  EqualTolerance = true
  ExtensionAngle = 0
  FormatSpec = ∅%.2w
  FormatSpecOverTolerance = %+.2w
  FormatSpecUnderTolerance = %+.2w
  Inverted = false
  LineAngle = 0
  LockPosition = false
  MeasureType = 1
  OverTolerance = 0
  References2D = -> [ProjItem004]
  Rotation = 0
  ScaleType = 0
  TheoreticalExact = false
  Type = 1
  UnderTolerance = 0
  X = -67.5529
  Y = 11.3782
FEATURE [TechDraw::DrawViewDimension] Dimension008
  AngleOverride = false
  Arbitrary = false
  ArbitraryTolerances = false
  EqualTolerance = true
  ExtensionAngle = 0
  FormatSpec = %.2w
  FormatSpecOverTolerance = %+.2w
  FormatSpecUnderTolerance = %+.2w
  Inverted = false
  LineAngle = 0
  LockPosition = false
  MeasureType = 1
  OverTolerance = 0
  References2D = -> [ProjItem003]
  Rotation = 0
  ScaleType = 0
  TheoreticalExact = false
  Type = 1
  UnderTolerance = 0
  X = -14.0084
  Y = 20.2922
FEATURE [TechDraw::DrawViewDimension] Dimension009
  AngleOverride = false
  Arbitrary = false
  ArbitraryTolerances = false
  EqualTolerance = true
  ExtensionAngle = 0
  FormatSpec = %.2w
  FormatSpecOverTolerance = %+.2w
  FormatSpecUnderTolerance = %+.2w
  Inverted = false
  LineAngle = 0
  LockPosition = false
  MeasureType = 1
  OverTolerance = 0
  References2D = -> [ProjItem003]
  Rotation = 0
  ScaleType = 0
  TheoreticalExact = false
  Type = 2
  UnderTolerance = 0
  X = -9.95885
  Y = 2.24165
FEATURE [TechDraw::DrawViewDimension] Dimension010
  AngleOverride = false
  Arbitrary = false
  ArbitraryTolerances = false
  EqualTolerance = true
  ExtensionAngle = 0
  FormatSpec = %.2w
  FormatSpecOverTolerance = %+.2w
  FormatSpecUnderTolerance = %+.2w
  Inverted = false
  LineAngle = 0
  LockPosition = false
  MeasureType = 1
  OverTolerance = 0
  References2D = -> [ProjItem003]
  Rotation = 0
  ScaleType = 0
  TheoreticalExact = false
  Type = 1
  UnderTolerance = 0
  X = 76.7667
  Y = 19.5172
FEATURE [TechDraw::DrawViewDimension] Dimension011
  AngleOverride = false
  Arbitrary = false
  ArbitraryTolerances = false
  EqualTolerance = true
  ExtensionAngle = 0
  FormatSpec = %.2w
  FormatSpecOverTolerance = %+.2w
  FormatSpecUnderTolerance = %+.2w
  Inverted = false
  LineAngle = 0
  LockPosition = false
  MeasureType = 1
  OverTolerance = 0
  References2D = -> [ProjItem003]
  Rotation = 0
  ScaleType = 0
  TheoreticalExact = false
  Type = 2
  UnderTolerance = 0
  X = 48.4911
  Y = 28.0499
FEATURE [TechDraw::DrawViewDimension] Dimension012
  AngleOverride = false
  Arbitrary = false
  ArbitraryTolerances = false
  EqualTolerance = true
  ExtensionAngle = 0
  FormatSpec = %.2w
  FormatSpecOverTolerance = %+.2w
  FormatSpecUnderTolerance = %+.2w
  Inverted = false
  LineAngle = 0
  LockPosition = false
  MeasureType = 1
  OverTolerance = 0
  References2D = -> [ProjItem003]
  Rotation = 0
  ScaleType = 0
  TheoreticalExact = false
  Type = 1
  UnderTolerance = 0
  X = -28.75
  Y = 30.3599
FEATURE [TechDraw::DrawViewDimension] Dimension013
  AngleOverride = false
  Arbitrary = false
  ArbitraryTolerances = false
  EqualTolerance = true
  ExtensionAngle = 0
  FormatSpec = %.2w
  FormatSpecOverTolerance = %+.2w
  FormatSpecUnderTolerance = %+.2w
  Inverted = false
  LineAngle = 0
  LockPosition = false
  MeasureType = 1
  OverTolerance = 0
  References2D = -> [ProjItem003]
  Rotation = 0
  ScaleType = 0
  TheoreticalExact = false
  Type = 2
  UnderTolerance = 0
  X = -39.6148
  Y = 10.1069
FEATURE [TechDraw::DrawViewDimension] Dimension014
  AngleOverride = false
  Arbitrary = false
  ArbitraryTolerances = false
  EqualTolerance = true
  ExtensionAngle = 0
  FormatSpec = %.2w
  FormatSpecOverTolerance = %+.2w
  FormatSpecUnderTolerance = %+.2w
  Inverted = false
  LineAngle = 0
  LockPosition = false
  MeasureType = 1
  OverTolerance = 0
  References2D = -> [ProjItem003]
  Rotation = 0
  ScaleType = 0
  TheoreticalExact = false
  Type = 1
  UnderTolerance = 0
  X = -29.1431
  Y = -24.0564
FEATURE [TechDraw::DrawViewDimension] Dimension015
  AngleOverride = false
  Arbitrary = false
  ArbitraryTolerances = false
  EqualTolerance = true
  ExtensionAngle = 0
  FormatSpec = %.2w
  FormatSpecOverTolerance = %+.2w
  FormatSpecUnderTolerance = %+.2w
  Inverted = false
  LineAngle = 0
  LockPosition = false
  MeasureType = 1
  OverTolerance = 0
  References2D = -> [ProjItem003]
  Rotation = 0
  ScaleType = 0
  TheoreticalExact = false
  Type = 2
  UnderTolerance = 0
  X = -17.9797
  Y = -13.0896
FEATURE [TechDraw::DrawViewDimension] Dimension016
  AngleOverride = false
  Arbitrary = false
  ArbitraryTolerances = false
  EqualTolerance = true
  ExtensionAngle = 0
  FormatSpec = %.2w
  FormatSpecOverTolerance = %+.2w
  FormatSpecUnderTolerance = %+.2w
  Inverted = false
  LineAngle = 0
  LockPosition = false
  MeasureType = 1
  OverTolerance = 0
  References2D = -> [ProjItem003]
  Rotation = 0
  ScaleType = 0
  TheoreticalExact = false
  Type = 1
  UnderTolerance = 0
  X = -62.4485
  Y = -16.3675
FEATURE [TechDraw::DrawViewDimension] Dimension017
  AngleOverride = false
  Arbitrary = false
  ArbitraryTolerances = false
  EqualTolerance = true
  ExtensionAngle = 0
  FormatSpec = %.2w
  FormatSpecOverTolerance = %+.2w
  FormatSpecUnderTolerance = %+.2w
  Inverted = false
  LineAngle = 0
  LockPosition = false
  MeasureType = 1
  OverTolerance = 0
  References2D = -> [ProjItem003]
  Rotation = 0
  ScaleType = 0
  TheoreticalExact = false
  Type = 2
  UnderTolerance = 0
  X = -78.1764
  Y = 2.64951
FEATURE [TechDraw::DrawViewDimension] Dimension018
  AngleOverride = false
  Arbitrary = false
  ArbitraryTolerances = false
  EqualTolerance = true
  ExtensionAngle = 0
  FormatSpec = %.2w
  FormatSpecOverTolerance = %+.2w
  FormatSpecUnderTolerance = %+.2w
  Inverted = false
  LineAngle = 0
  LockPosition = false
  MeasureType = 1
  OverTolerance = 0
  References2D = -> [ProjItem003]
  Rotation = 0
  ScaleType = 0
  TheoreticalExact = false
  Type = 1
  UnderTolerance = 0
  X = -78.4717
  Y = 17.7915
FEATURE [TechDraw::DrawViewDimension] Dimension019
  AngleOverride = false
  Arbitrary = false
  ArbitraryTolerances = false
  EqualTolerance = true
  ExtensionAngle = 0
  FormatSpec = %.2w
  FormatSpecOverTolerance = %+.2w
  FormatSpecUnderTolerance = %+.2w
  Inverted = false
  LineAngle = 0
  LockPosition = false
  MeasureType = 1
  OverTolerance = 0
  References2D = -> [ProjItem003]
  Rotation = 0
  ScaleType = 0
  TheoreticalExact = false
  Type = 1
  UnderTolerance = 0
  X = -61.8754
  Y = 17.9721
FEATURE [TechDraw::DrawViewDimension] Dimension020
  AngleOverride = false
  Arbitrary = false
  ArbitraryTolerances = false
  EqualTolerance = true
  ExtensionAngle = 0
  FormatSpec = %.2w
  FormatSpecOverTolerance = %+.2w
  FormatSpecUnderTolerance = %+.2w
  Inverted = false
  LineAngle = 0
  LockPosition = false
  MeasureType = 1
  OverTolerance = 0
  References2D = -> [ProjItem003]
  Rotation = 0
  ScaleType = 0
  TheoreticalExact = false
  Type = 2
  UnderTolerance = 0
  X = -47.8918
  Y = 15.0311
FEATURE [TechDraw::DrawViewDimension] Dimension021
  AngleOverride = false
  Arbitrary = false
  ArbitraryTolerances = false
  EqualTolerance = true
  ExtensionAngle = 0
  FormatSpec = %.2w
  FormatSpecOverTolerance = %+.2w
  FormatSpecUnderTolerance = %+.2w
  Inverted = false
  LineAngle = 0
  LockPosition = false
  MeasureType = 1
  OverTolerance = 0
  References2D = -> [ProjItem003]
  Rotation = 0
  ScaleType = 0
  TheoreticalExact = false
  Type = 1
  UnderTolerance = 0
  X = -55.2
  Y = 25.7033
FEATURE [TechDraw::DrawViewDimension] Dimension022
  AngleOverride = false
  Arbitrary = false
  ArbitraryTolerances = false
  EqualTolerance = true
  ExtensionAngle = 0
  FormatSpec = %.2w
  FormatSpecOverTolerance = %+.2w
  FormatSpecUnderTolerance = %+.2w
  Inverted = false
  LineAngle = 0
  LockPosition = false
  MeasureType = 1
  OverTolerance = 0
  References2D = -> [ProjItem003]
  Rotation = 0
  ScaleType = 0
  TheoreticalExact = false
  Type = 2
  UnderTolerance = 0
  X = -47.5574
  Y = -10.7328
FEATURE [TechDraw::DrawPage] Page002  label="Soporte de Botones Atrás"
  KeepUpdated = true
  NextBalloonIndex = 1
  ProjectionType = 0
  Template = -> Template002
  Views = -> [ProjGroup002,Symbol,Dimension,Dimension001,Dimension002,Dimension003,Dimension004,Dimension005,Dimension006,Dimension007,Dimension008,Dimension009,Dimension010,Dimension011,Dimension012,Dimension013,Dimension014,Dimension015,Dimension016,Dimension017,Dimension018,Dimension019,Dimension020,Dimension021,Dimension022]
